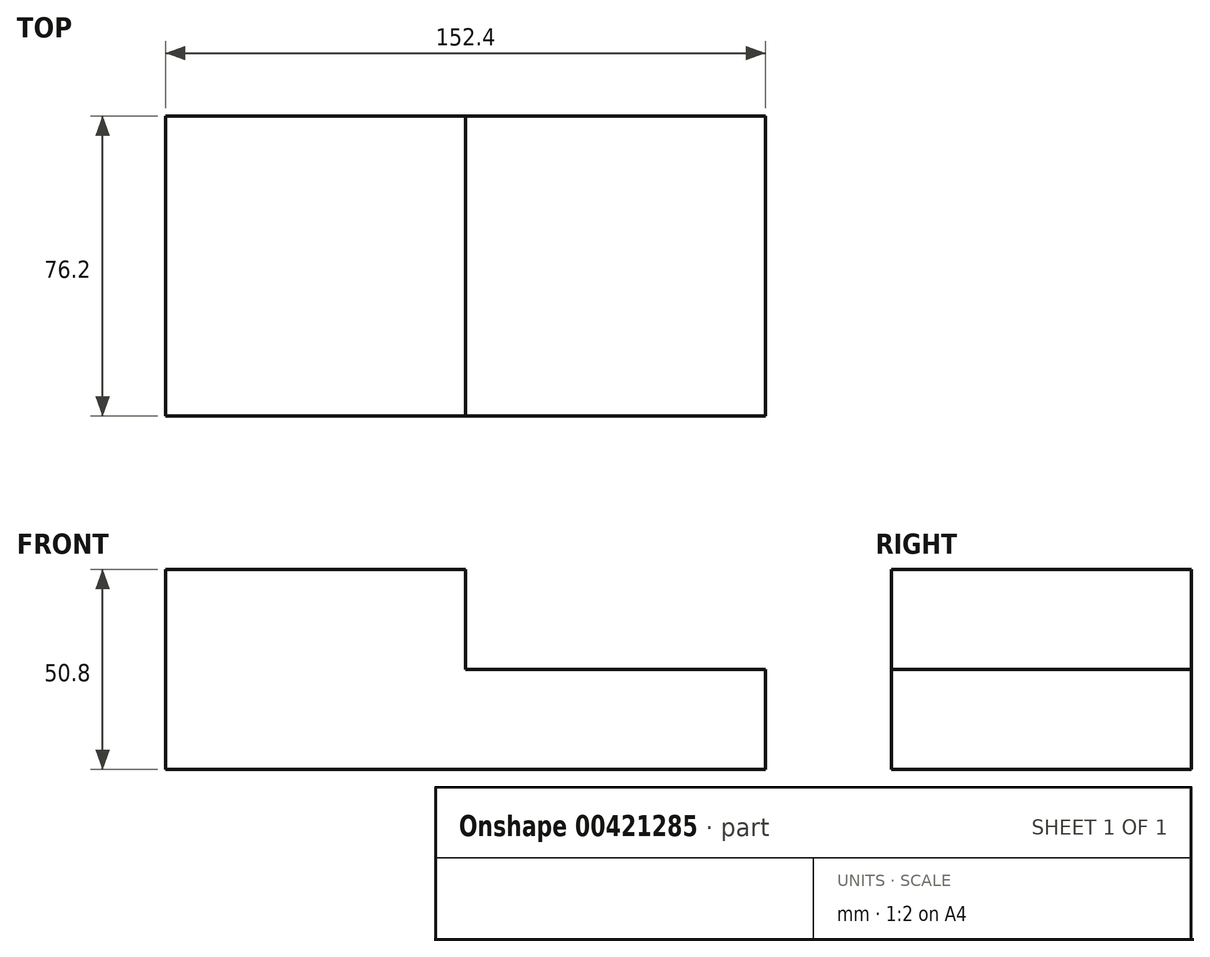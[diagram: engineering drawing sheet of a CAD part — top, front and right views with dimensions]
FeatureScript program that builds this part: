
annotation { "Feature Type Name" : "Feature", "Feature Type Description" : "" }
export const myFeature = defineFeature(function(context is Context, id is Id, definition is map)
    precondition{}
    {
        {
            var Q0;
            Q0=qCreatedBy(makeId("Front.planeOp"),FACE);
            var sketch = newSketch(context, id + "F0", { "sketchPlane" : qUnion([Q0])});
            skLineSegment(sketch, "E0", {"start": v(0, 0) * mm, "end": v(0, -50.8) * mm});
            skLineSegment(sketch, "E1", {"start": v(0, -50.8) * mm, "end": v(152.4, -50.8) * mm});
            skLineSegment(sketch, "E2", {"start": v(152.4, -50.8) * mm, "end": v(152.4, -25.4) * mm});
            skLineSegment(sketch, "E3", {"start": v(152.4, -25.4) * mm, "end": v(76.2, -25.4) * mm});
            skLineSegment(sketch, "E4", {"start": v(76.2, -25.4) * mm, "end": v(76.2, 0) * mm});
            skLineSegment(sketch, "E5", {"start": v(76.2, 0) * mm, "end": v(76.2, 0) * mm});
            skLineSegment(sketch, "E6", {"start": v(76.2, 0) * mm, "end": v(0, 0) * mm});
            skSolve(sketch);
        }
        {
            var Q0;
            Q0=makeQuery(id+"F0.imprint","IMPRINT",FACE,{"disambiguationData":[TD([[makeQuery(id+"F0.imprint","IMPRINT",EDGE,{"derivedFrom":sQuery(id+"F0.wireOp",EDGE,"E0")}),1.0]])]});
            extrude(context, id + "F1", {"entities" : qUnion([Q0]), "depth" : 76.2 * mm});
        }
    });
